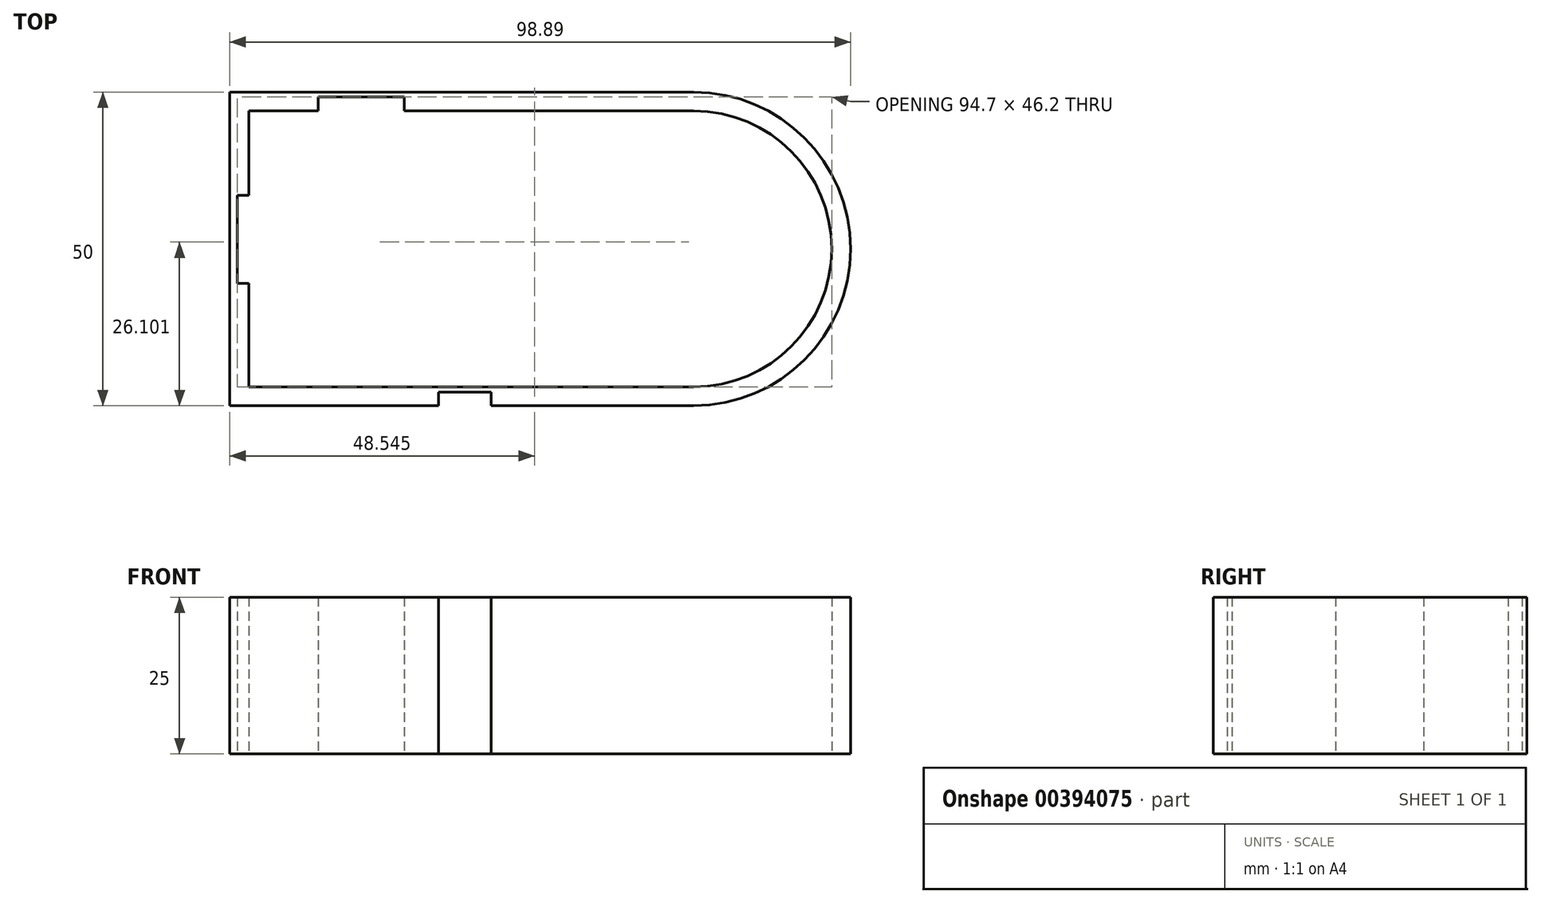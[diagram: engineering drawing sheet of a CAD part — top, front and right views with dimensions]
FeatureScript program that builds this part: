
annotation { "Feature Type Name" : "Feature", "Feature Type Description" : "" }
export const myFeature = defineFeature(function(context is Context, id is Id, definition is map)
    precondition{}
    {
        {
            var Q0;
            Q0=qCreatedBy(makeId("Top.planeOp"),FACE);
            var sketch = newSketch(context, id + "F0", { "sketchPlane" : qUnion([Q0])});
            skLineSegment(sketch, "E0.bottom", {"start": v(-48.53, 11.2) * mm, "end": v(-30.05, 11.2) * mm});
            skLineSegment(sketch, "E0.top", {"start": v(-48.53, -38.8) * mm, "end": v(-15.3, -38.8) * mm});
            skLineSegment(sketch, "E0.left", {"start": v(-48.53, 11.2) * mm, "end": v(-48.53, -38.8) * mm});
            skArc(sketch, "E1", {"start": v(25.36, -38.8) * mm, "mid": v(50.36, -13.8) * mm, "end": v(25.36, 11.2) * mm});
            skPoint(sketch, "E1.centerSnap0", {"position": v(51.47, -13.8) * mm});
            skPoint(sketch, "E2.orphan", {"position": v(51.47, 11.2) * mm});
            skPoint(sketch, "E3.orphan", {"position": v(51.47, -38.8) * mm});
            skLineSegment(sketch, "E4.0", {"start": v(-45.53, 8.2) * mm, "end": v(-34.46, 8.2) * mm});
            skLineSegment(sketch, "E4.1", {"start": v(-45.53, 8.2) * mm, "end": v(-45.53, -5.25) * mm});
            skLineSegment(sketch, "E4.2", {"start": v(-45.53, -35.8) * mm, "end": v(25.36, -35.8) * mm});
            skArc(sketch, "E4.3", {"start": v(25.36, -35.8) * mm, "mid": v(47.36, -13.8) * mm, "end": v(25.36, 8.2) * mm});
            skLineSegment(sketch, "E5.bottom", {"start": v(-45.53, -5.25) * mm, "end": v(-47.33, -5.25) * mm});
            skLineSegment(sketch, "E5.top", {"start": v(-45.53, -19.3) * mm, "end": v(-47.33, -19.3) * mm});
            skLineSegment(sketch, "E5.right", {"start": v(-47.33, -5.25) * mm, "end": v(-47.33, -19.3) * mm});
            skLineSegment(sketch, "E6.trimOffspring", {"start": v(-45.53, -19.3) * mm, "end": v(-45.53, -35.8) * mm});
            skLineSegment(sketch, "E7.top", {"start": v(-15.3, -36.6) * mm, "end": v(-6.91, -36.6) * mm});
            skLineSegment(sketch, "E7.left", {"start": v(-15.3, -38.8) * mm, "end": v(-15.3, -36.6) * mm});
            skLineSegment(sketch, "E7.right", {"start": v(-6.91, -38.8) * mm, "end": v(-6.91, -36.6) * mm});
            skLineSegment(sketch, "E8.trimOffspring", {"start": v(-19.37, 11.2) * mm, "end": v(25.36, 11.2) * mm});
            skLineSegment(sketch, "E9.trimOffspring", {"start": v(-6.91, -38.8) * mm, "end": v(25.36, -38.8) * mm});
            skLineSegment(sketch, "E10", {"start": v(-30.05, 11.2) * mm, "end": v(-19.37, 11.2) * mm});
            skLineSegment(sketch, "E11.top", {"start": v(-20.74, 10.4) * mm, "end": v(-34.46, 10.4) * mm});
            skLineSegment(sketch, "E11.left", {"start": v(-20.74, 8.2) * mm, "end": v(-20.74, 10.4) * mm});
            skLineSegment(sketch, "E11.right", {"start": v(-34.46, 8.2) * mm, "end": v(-34.46, 10.4) * mm});
            skLineSegment(sketch, "E12.trimOffspring", {"start": v(-20.74, 8.2) * mm, "end": v(25.36, 8.2) * mm});
            skSolve(sketch);
        }
        {
            var Q0;
            Q0 = qSketchRegion(id + "F0", true);
            extrude(context, id + "F1", {"entities" : qUnion([Q0]), "depth" : 25 * mm});
        }
    });
